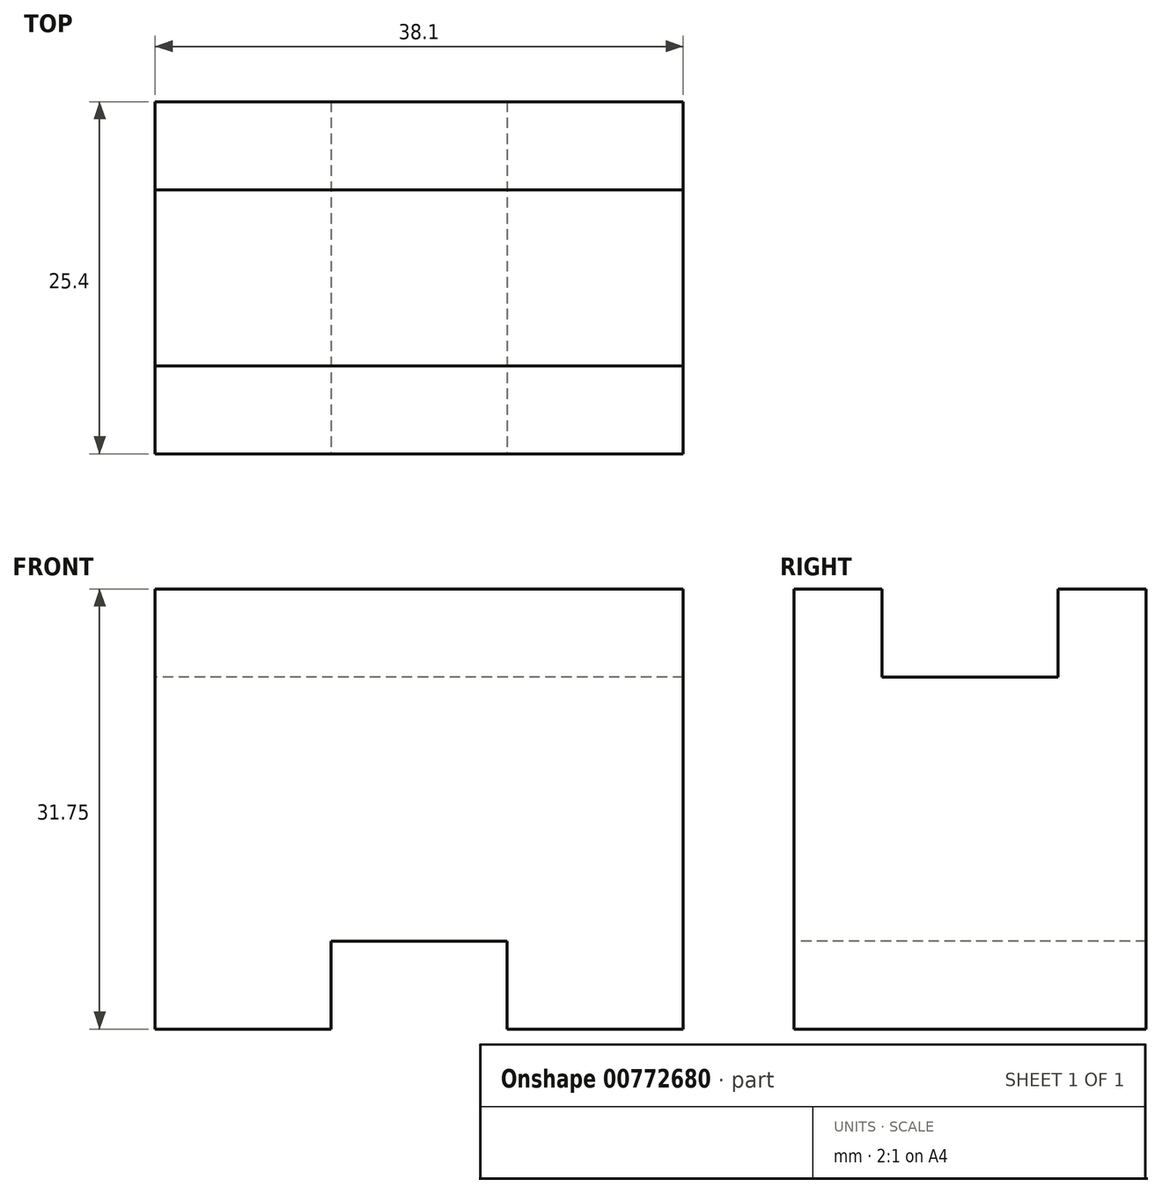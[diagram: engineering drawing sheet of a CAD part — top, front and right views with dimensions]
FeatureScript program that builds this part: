
annotation { "Feature Type Name" : "Feature", "Feature Type Description" : "" }
export const myFeature = defineFeature(function(context is Context, id is Id, definition is map)
    precondition{}
    {
        {
            var Q0;
            Q0=qCreatedBy(makeId("Front.planeOp"),FACE);
            var sketch = newSketch(context, id + "F0", { "sketchPlane" : qUnion([Q0])});
            skLineSegment(sketch, "E0", {"start": v(0, 0) * mm, "end": v(38.1, 0) * mm});
            skLineSegment(sketch, "E1", {"start": v(38.1, 0) * mm, "end": v(38.1, 31.75) * mm});
            skLineSegment(sketch, "E2", {"start": v(38.1, 31.75) * mm, "end": v(0, 31.75) * mm});
            skLineSegment(sketch, "E3", {"start": v(0, 31.75) * mm, "end": v(0, 0) * mm});
            skSolve(sketch);
        }
        {
            var Q0;
            Q0=makeQuery(id+"F0.imprint","IMPRINT",FACE,{"disambiguationData":[TD([[makeQuery(id+"F0.imprint","IMPRINT",EDGE,{"derivedFrom":sQuery(id+"F0.wireOp",EDGE,"E0")}),1.0]])]});
            extrude(context, id + "F1", {"entities" : qUnion([Q0]), "depth" : 25.4 * mm, "offsetDistance" : 25.4 * mm});
        }
        {
            var Q0;
            Q0=makeQuery(id+"F1.opExtrude","CAP_FACE",FACE,{"disambiguationData":[OSD([sQuery(id+"F0.wireOp",EDGE,"E0"),sQuery(id+"F0.wireOp",EDGE,"E1"),sQuery(id+"F0.wireOp",EDGE,"E2"),sQuery(id+"F0.wireOp",EDGE,"E3")])],"isStart":false});
            var sketch = newSketch(context, id + "F2", { "sketchPlane" : qUnion([Q0])});
            skLineSegment(sketch, "E4", {"start": v(0, 0) * mm, "end": v(12.7, 0) * mm});
            skLineSegment(sketch, "E5", {"start": v(12.7, 0) * mm, "end": v(12.7, 6.35) * mm});
            skLineSegment(sketch, "E6", {"start": v(12.7, 6.35) * mm, "end": v(25.4, 6.35) * mm});
            skLineSegment(sketch, "E7", {"start": v(25.4, 6.35) * mm, "end": v(25.4, 0) * mm});
            skLineSegment(sketch, "E8", {"start": v(25.4, 0) * mm, "end": v(12.7, 0) * mm});
            skLineSegment(sketch, "E9", {"start": v(25.4, 0) * mm, "end": v(38.1, 0) * mm});
            skSolve(sketch);
        }
        {
            var Q0;
            Q0=makeQuery(id+"F2.imprint","IMPRINT",FACE,{"disambiguationData":[TD([[makeQuery(id+"F2.imprint","IMPRINT",EDGE,{"derivedFrom":sQuery(id+"F2.wireOp",EDGE,"E5")}),-1.0]])]});
            extrude(context, id + "F3", {"entities" : qUnion([Q0]), "operationType" : NewBodyOperationType.REMOVE, "oppositeDirection" : true, "depth" : 25.4 * mm, "offsetDistance" : 25.4 * mm});
        }
        {
            var Q0;
            Q0=makeQuery(id+"F1.opExtrude","SWEPT_FACE",FACE,{"disambiguationData":[OSD([sQuery(id+"F0.wireOp",EDGE,"E2")])]});
            var sketch = newSketch(context, id + "F4", { "sketchPlane" : qUnion([Q0])});
            skLineSegment(sketch, "E10", {"start": v(38.1, -25.4) * mm, "end": v(38.1, -19.05) * mm});
            skLineSegment(sketch, "E11", {"start": v(38.1, -19.05) * mm, "end": v(38.1, -6.35) * mm});
            skLineSegment(sketch, "E12", {"start": v(38.1, -6.35) * mm, "end": v(38.1, 0) * mm});
            skLineSegment(sketch, "E13", {"start": v(38.1, 0) * mm, "end": v(38.1, -6.35) * mm});
            skLineSegment(sketch, "E14", {"start": v(38.1, -6.35) * mm, "end": v(0, -6.35) * mm});
            skLineSegment(sketch, "E15", {"start": v(0, -6.35) * mm, "end": v(0, 0) * mm});
            skLineSegment(sketch, "E16", {"start": v(0, 0) * mm, "end": v(38.1, 0) * mm});
            skLineSegment(sketch, "E17", {"start": v(38.1, -19.05) * mm, "end": v(0, -19.05) * mm});
            skLineSegment(sketch, "E18", {"start": v(0, -19.05) * mm, "end": v(0, -25.4) * mm});
            skLineSegment(sketch, "E19", {"start": v(0, -25.4) * mm, "end": v(38.1, -25.4) * mm});
            skSolve(sketch);
        }
        {
            var Q0;
            Q0=makeQuery(id+"F4.imprint","IMPRINT",FACE,{"disambiguationData":[TD([[makeQuery(id+"F4.imprint","IMPRINT",EDGE,{"derivedFrom":sQuery(id+"F4.wireOp",EDGE,"E11")}),1.0]])]});
            extrude(context, id + "F5", {"entities" : qUnion([Q0]), "operationType" : NewBodyOperationType.REMOVE, "oppositeDirection" : true, "depth" : 6.35 * mm, "offsetDistance" : 25.4 * mm});
        }
    });
